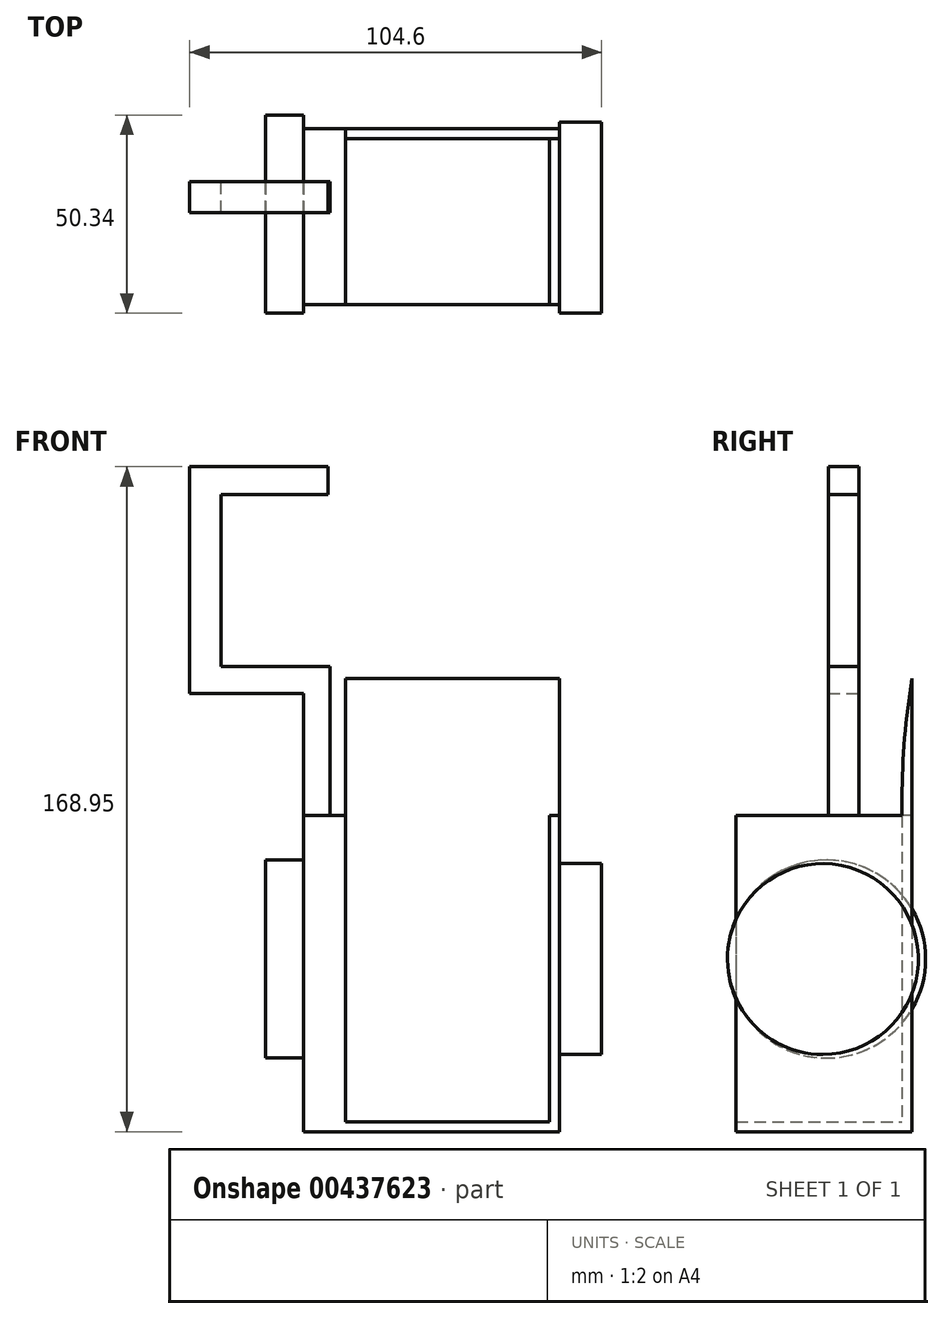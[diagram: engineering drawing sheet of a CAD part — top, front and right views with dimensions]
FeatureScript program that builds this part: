
annotation { "Feature Type Name" : "Feature", "Feature Type Description" : "" }
export const myFeature = defineFeature(function(context is Context, id is Id, definition is map)
    precondition{}
    {
        {
            var Q0;
            Q0=qCreatedBy(makeId("Front.planeOp"),FACE);
            var sketch = newSketch(context, id + "F0", { "sketchPlane" : qUnion([Q0])});
            skLineSegment(sketch, "E0.bottom", {"start": v(-6.67, 36.45) * mm, "end": v(58.31, 36.45) * mm});
            skLineSegment(sketch, "E0.top", {"start": v(-6.67, -43.86) * mm, "end": v(58.31, -43.86) * mm});
            skLineSegment(sketch, "E0.left", {"start": v(-6.67, 36.45) * mm, "end": v(-6.67, -43.86) * mm});
            skLineSegment(sketch, "E0.right", {"start": v(58.31, 36.45) * mm, "end": v(58.31, -43.86) * mm});
            skSolve(sketch);
        }
        {
            var Q0;
            Q0=makeQuery(id+"F0.imprint","IMPRINT",FACE,{"disambiguationData":[TD([[makeQuery(id+"F0.imprint","IMPRINT",EDGE,{"derivedFrom":sQuery(id+"F0.wireOp",EDGE,"E0.bottom")}),-1.0]])]});
            extrude(context, id + "F1", {"entities" : qUnion([Q0]), "depth" : 44.7 * mm});
        }
        {
            var Q0;
            Q0=makeQuery(id+"F1.opExtrude","SWEPT_FACE",FACE,{"disambiguationData":[OSD([sQuery(id+"F0.wireOp",EDGE,"E0.bottom")])]});
            var Q1;
            Q1=makeQuery(id+"F1.opExtrude","CAP_FACE",FACE,{"disambiguationData":[OSD([sQuery(id+"F0.wireOp",EDGE,"E0.bottom"),sQuery(id+"F0.wireOp",EDGE,"E0.top"),sQuery(id+"F0.wireOp",EDGE,"E0.left"),sQuery(id+"F0.wireOp",EDGE,"E0.right")])],"isStart":false});
            shell(context, id + "F2", {"entities" : qUnion([Q0, Q1]), "thickness" : 2.54 * mm});
        }
        {
            var Q0;
            Q0=makeQuery(id+"F1.opExtrude","SWEPT_FACE",FACE,{"disambiguationData":[OSD([sQuery(id+"F0.wireOp",EDGE,"E0.right")])]});
            var sketch = newSketch(context, id + "F3", { "sketchPlane" : qUnion([Q0])});
            skCircle(sketch, "E1", {"center": v(-22.66, 0) * mm, "radius": 24.24 * mm});
            skSolve(sketch);
        }
        {
            var Q0;
            Q0 = qSketchRegion(id + "F3", true);
            var Q1;
            Q1=makeQuery(id+"F1.opExtrude","SWEPT_FACE",FACE,{"disambiguationData":[OSD([sQuery(id+"F0.wireOp",EDGE,"E0.left")])]});
            extrude(context, id + "F4", {"entities" : qUnion([Q0, Q1]), "operationType" : NewBodyOperationType.ADD, "depth" : 10.67 * mm});
        }
        {
            var Q0;
            Q0=makeQuery(id+"F1.opExtrude","SWEPT_FACE",FACE,{"disambiguationData":[OSD([sQuery(id+"F0.wireOp",EDGE,"E0.left")])]});
            var sketch = newSketch(context, id + "F5", { "sketchPlane" : qUnion([Q0])});
            skCircle(sketch, "E2", {"center": v(21.72, 0) * mm, "radius": 25.16 * mm});
            skSolve(sketch);
        }
        {
            var Q0;
            Q0 = qSketchRegion(id + "F5", true);
            extrude(context, id + "F6", {"entities" : qUnion([Q0]), "operationType" : NewBodyOperationType.ADD, "depth" : 9.65 * mm});
        }
        {
            var Q0;
            {var subQ0=sQuery(id+"F0.wireOp",EDGE,"E0.bottom");Q0=makeQuery(id+"F4.boolean.opBoolean","MERGE",FACE,{"derivedFrom":[makeQuery(id+"F1.opExtrude","SWEPT_FACE",FACE,{"disambiguationData":[OSD([subQ0])]}),makeQuery(id+"F4.opExtrude","SWEPT_FACE",FACE,{"disambiguationData":[OSD([subQ0,sQuery(id+"F0.wireOp",EDGE,"E0.left")])]})]});}
            var sketch = newSketch(context, id + "F7", { "sketchPlane" : qUnion([Q0])});
            skLineSegment(sketch, "E3.bottom", {"start": v(0, -21.3) * mm, "end": v(-6.67, -21.3) * mm});
            skLineSegment(sketch, "E3.top", {"start": v(0, -13.53) * mm, "end": v(-6.67, -13.53) * mm});
            skLineSegment(sketch, "E3.left", {"start": v(0, -21.3) * mm, "end": v(0, -13.53) * mm});
            skLineSegment(sketch, "E3.right", {"start": v(-6.67, -21.3) * mm, "end": v(-6.67, -13.53) * mm});
            skSolve(sketch);
        }
        {
            var Q0;
            Q0=makeQuery(id+"F7.imprint","IMPRINT",FACE,{"disambiguationData":[TD([[makeQuery(id+"F7.imprint","IMPRINT",EDGE,{"derivedFrom":sQuery(id+"F7.wireOp",EDGE,"E3.bottom")}),-1.0]])]});
            extrude(context, id + "F8", {"entities" : qUnion([Q0]), "operationType" : NewBodyOperationType.ADD, "depth" : 37.85 * mm});
        }
        {
            var Q0;
            {var subQ0=sQuery(id+"F0.wireOp",EDGE,"E0.left");var subQ1=sQuery(id+"F0.wireOp",EDGE,"E0.bottom");Q0=makeQuery(id+"F8.boolean.opBoolean","MERGE",FACE,{"derivedFrom":[makeQuery(id+"F6.boolean.opBoolean","SPLIT",FACE,{"disambiguationData":[TD([makeQuery(id+"F1.opExtrude","SWEPT_FACE",FACE,{"disambiguationData":[OSD([subQ1])]})])],"derivedFrom":makeQuery(id+"F1.opExtrude","SWEPT_FACE",FACE,{"disambiguationData":[OSD([subQ0])]})}),makeQuery(id+"F8.opExtrude","SWEPT_FACE",FACE,{"disambiguationData":[OSD([sQuery(id+"F7.wireOp",EDGE,"E3.right")])]})]});}
            var sketch = newSketch(context, id + "F9", { "sketchPlane" : qUnion([Q0])});
            skLineSegment(sketch, "E4.bottom", {"start": v(21.3, 74.3) * mm, "end": v(13.53, 74.3) * mm});
            skLineSegment(sketch, "E4.top", {"start": v(21.3, 67.45) * mm, "end": v(13.53, 67.45) * mm});
            skLineSegment(sketch, "E4.left", {"start": v(21.3, 74.3) * mm, "end": v(21.3, 67.45) * mm});
            skLineSegment(sketch, "E4.right", {"start": v(13.53, 74.3) * mm, "end": v(13.53, 67.45) * mm});
            skSolve(sketch);
        }
        {
            var Q0;
            Q0 = qSketchRegion(id + "F9", true);
            extrude(context, id + "F10", {"entities" : qUnion([Q0]), "operationType" : NewBodyOperationType.ADD, "depth" : 28.96 * mm});
        }
        {
            var Q0;
            Q0=makeQuery(id+"F10.boolean.opBoolean","MERGE",FACE,{"derivedFrom":[makeQuery(id+"F8.opExtrude","CAP_FACE",FACE,{"disambiguationData":[OSD([sQuery(id+"F7.wireOp",EDGE,"E3.bottom"),sQuery(id+"F7.wireOp",EDGE,"E3.top"),sQuery(id+"F7.wireOp",EDGE,"E3.left"),sQuery(id+"F7.wireOp",EDGE,"E3.right")])],"isStart":false}),makeQuery(id+"F10.opExtrude","SWEPT_FACE",FACE,{"disambiguationData":[OSD([sQuery(id+"F9.wireOp",EDGE,"E4.bottom")])]})]});
            var sketch = newSketch(context, id + "F11", { "sketchPlane" : qUnion([Q0])});
            skLineSegment(sketch, "E5.bottom", {"start": v(-35.62, -21.3) * mm, "end": v(-27.73, -21.3) * mm});
            skLineSegment(sketch, "E5.top", {"start": v(-35.62, -13.53) * mm, "end": v(-27.73, -13.53) * mm});
            skLineSegment(sketch, "E5.left", {"start": v(-35.62, -21.3) * mm, "end": v(-35.62, -13.53) * mm});
            skLineSegment(sketch, "E5.right", {"start": v(-27.73, -21.3) * mm, "end": v(-27.73, -13.53) * mm});
            skSolve(sketch);
        }
        {
            var Q0;
            Q0=makeQuery(id+"F11.imprint","IMPRINT",FACE,{"disambiguationData":[TD([[makeQuery(id+"F11.imprint","IMPRINT",EDGE,{"derivedFrom":sQuery(id+"F11.wireOp",EDGE,"E5.bottom")}),-1.0]])]});
            extrude(context, id + "F12", {"entities" : qUnion([Q0]), "operationType" : NewBodyOperationType.ADD, "depth" : 25.4 * mm});
        }
        {
            var Q0;
            Q0=makeQuery(id+"F12.opExtrude","CAP_FACE",FACE,{"disambiguationData":[OSD([sQuery(id+"F11.wireOp",EDGE,"E5.bottom"),sQuery(id+"F11.wireOp",EDGE,"E5.top"),sQuery(id+"F11.wireOp",EDGE,"E5.left"),sQuery(id+"F11.wireOp",EDGE,"E5.right")])],"isStart":false});
            extrude(context, id + "F13", {"entities" : qUnion([Q0]), "operationType" : NewBodyOperationType.ADD, "depth" : 25.4 * mm});
        }
        {
            var Q0;
            {var subQ0=sQuery(id+"F0.wireOp",EDGE,"E0.bottom");Q0=makeQuery(id+"F4.boolean.opBoolean","MERGE",FACE,{"derivedFrom":[makeQuery(id+"F1.opExtrude","SWEPT_FACE",FACE,{"disambiguationData":[OSD([subQ0])]}),makeQuery(id+"F4.opExtrude","SWEPT_FACE",FACE,{"disambiguationData":[OSD([subQ0,sQuery(id+"F0.wireOp",EDGE,"E0.left")])]})]});}
            var sketch = newSketch(context, id + "F14", { "sketchPlane" : qUnion([Q0])});
            skLineSegment(sketch, "E6.bottom", {"start": v(58.31, 0) * mm, "end": v(4, 0) * mm});
            skLineSegment(sketch, "E6.top", {"start": v(58.31, -2.54) * mm, "end": v(4, -2.54) * mm});
            skLineSegment(sketch, "E6.left", {"start": v(58.31, 0) * mm, "end": v(58.31, -2.54) * mm});
            skLineSegment(sketch, "E6.right", {"start": v(4, 0) * mm, "end": v(4, -2.54) * mm});
            skSolve(sketch);
        }
        {
            var Q0;
            Q0=makeQuery(id+"F14.imprint","IMPRINT",FACE,{"disambiguationData":[TD([[makeQuery(id+"F14.imprint","IMPRINT",EDGE,{"derivedFrom":sQuery(id+"F14.wireOp",EDGE,"E6.bottom")}),-1.0]])]});
            extrude(context, id + "F15", {"entities" : qUnion([Q0]), "operationType" : NewBodyOperationType.ADD, "depth" : 34.8 * mm});
        }
        {
            var Q0;
            Q0=makeQuery(id+"F15.opExtrude","CAP_EDGE",EDGE,{"disambiguationData":[OSD([sQuery(id+"F14.wireOp",EDGE,"E6.top")])],"isStart":false});
            fillet(context, id + "F16", {"entities" : qUnion([Q0]), "radius" : 181.5 * mm, "tangentPropagation" : true, "allowEdgeOverflow" : false});
        }
        {
            var Q0;
            {var subQ0=sQuery(id+"F11.wireOp",EDGE,"E5.right");Q0=makeQuery(id+"F13.boolean.opBoolean","MERGE",FACE,{"derivedFrom":[makeQuery(id+"F12.opExtrude","SWEPT_FACE",FACE,{"disambiguationData":[OSD([subQ0])]}),makeQuery(id+"F13.opExtrude","SWEPT_FACE",FACE,{"disambiguationData":[OSD([subQ0])]})]});}
            var sketch = newSketch(context, id + "F17", { "sketchPlane" : qUnion([Q0])});
            skLineSegment(sketch, "E7.bottom", {"start": v(-13.53, 125.1) * mm, "end": v(-21.3, 125.1) * mm});
            skLineSegment(sketch, "E7.top", {"start": v(-13.53, 117.96) * mm, "end": v(-21.3, 117.96) * mm});
            skLineSegment(sketch, "E7.left", {"start": v(-13.53, 125.1) * mm, "end": v(-13.53, 117.96) * mm});
            skLineSegment(sketch, "E7.right", {"start": v(-21.3, 125.1) * mm, "end": v(-21.3, 117.96) * mm});
            skSolve(sketch);
        }
        {
            var Q0;
            Q0 = qSketchRegion(id + "F17", true);
            extrude(context, id + "F18", {"entities" : qUnion([Q0]), "operationType" : NewBodyOperationType.ADD, "depth" : 27.18 * mm});
        }
    });
